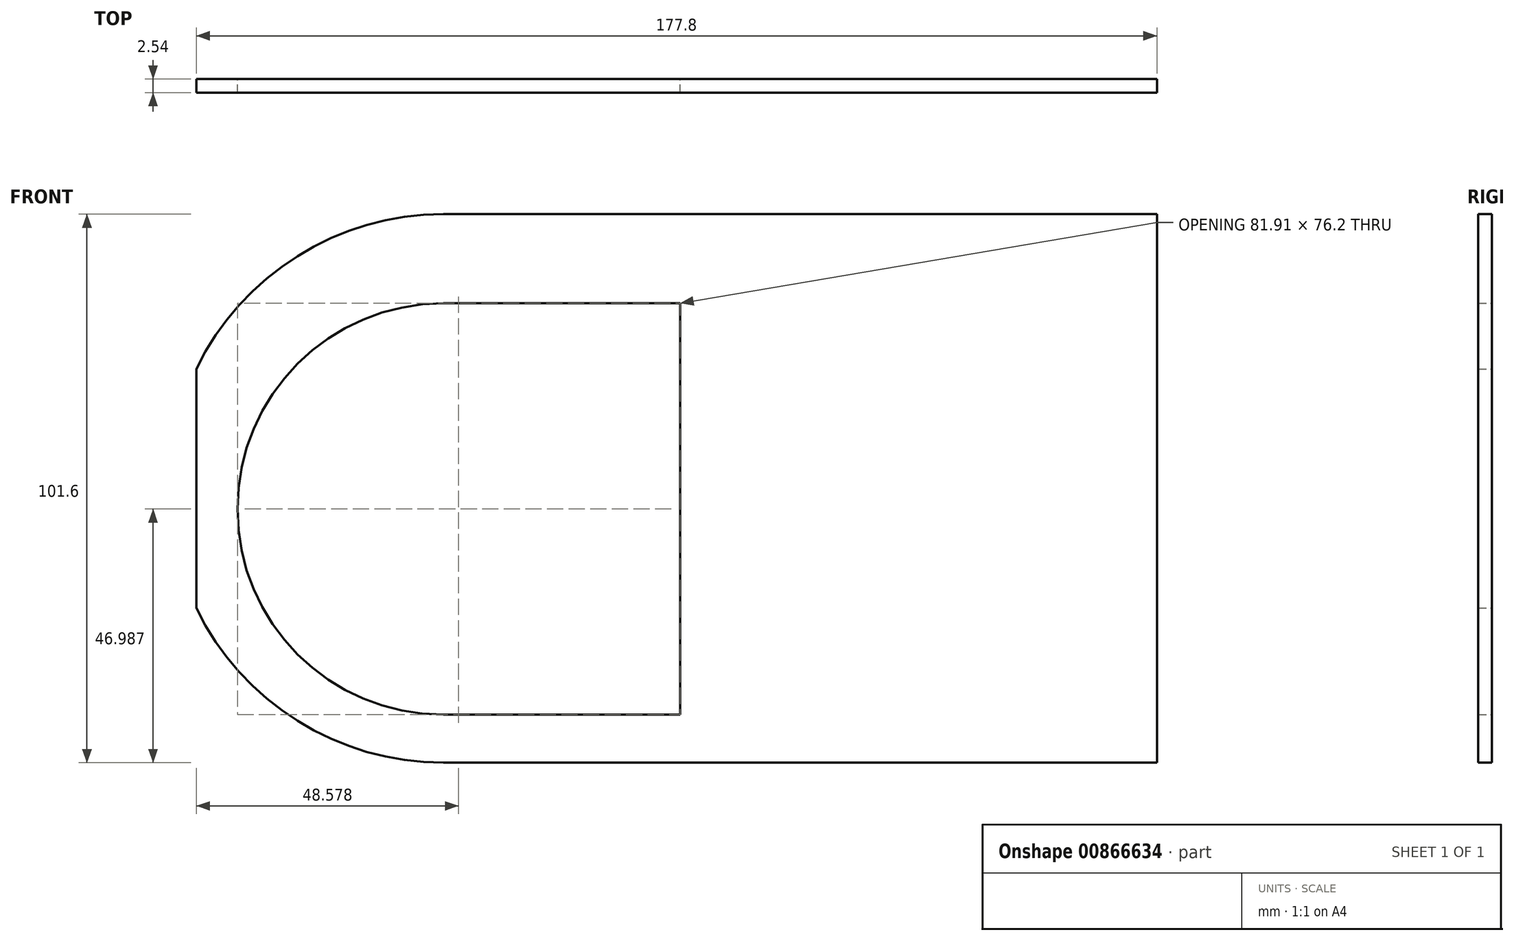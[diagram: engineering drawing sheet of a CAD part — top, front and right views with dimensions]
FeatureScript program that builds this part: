
annotation { "Feature Type Name" : "Feature", "Feature Type Description" : "" }
export const myFeature = defineFeature(function(context is Context, id is Id, definition is map)
    precondition{}
    {
        {
            var Q0;
            Q0=qCreatedBy(makeId("Front.planeOp"),FACE);
            var sketch = newSketch(context, id + "F0", { "sketchPlane" : qUnion([Q0])});
            skArc(sketch, "E0.0", {"start": v(-45.72, -14.87) * mm, "mid": v(-26.98, -35.77) * mm, "end": v(0, -43.52) * mm});
            skLineSegment(sketch, "E1.bottom", {"start": v(0, -43.52) * mm, "end": v(132.08, -43.52) * mm});
            skLineSegment(sketch, "E1.top", {"start": v(0, 58.08) * mm, "end": v(132.08, 58.08) * mm});
            skLineSegment(sketch, "E1.right", {"start": v(132.08, -43.52) * mm, "end": v(132.08, 58.08) * mm});
            skLineSegment(sketch, "E2.right", {"start": v(-45.72, 29.42) * mm, "end": v(-45.72, -14.87) * mm});
            skArc(sketch, "E3.trimOffspring", {"start": v(0, 58.08) * mm, "mid": v(-26.98, 50.32) * mm, "end": v(-45.72, 29.42) * mm});
            skArc(sketch, "E4", {"start": v(0, 41.57) * mm, "mid": v(-38.1, 3.47) * mm, "end": v(0, -34.63) * mm});
            skLineSegment(sketch, "E5", {"start": v(0, 41.57) * mm, "end": v(43.82, 41.57) * mm});
            skLineSegment(sketch, "E6", {"start": v(0, -34.63) * mm, "end": v(43.82, -34.63) * mm});
            skPoint(sketch, "E7.center.orphan", {"position": v(87.63, 3.47) * mm});
            skLineSegment(sketch, "E8", {"start": v(43.81, -34.63) * mm, "end": v(43.81, 41.57) * mm});
            skPoint(sketch, "E9.orphan", {"position": v(87.63, 41.57) * mm});
            skPoint(sketch, "E10.orphan", {"position": v(87.63, -34.63) * mm});
            skCircle(sketch, "E11", {"center": v(0, 3.47) * mm, "radius": 38.1 * mm});
            skSolve(sketch);
        }
        {
            var Q0;
            Q0 = qSketchRegion(id + "F0", true);
            extrude(context, id + "F1", {"entities" : qUnion([Q0]), "depth" : 2.54 * mm, "offsetDistance" : 25.4 * mm});
        }
    });
